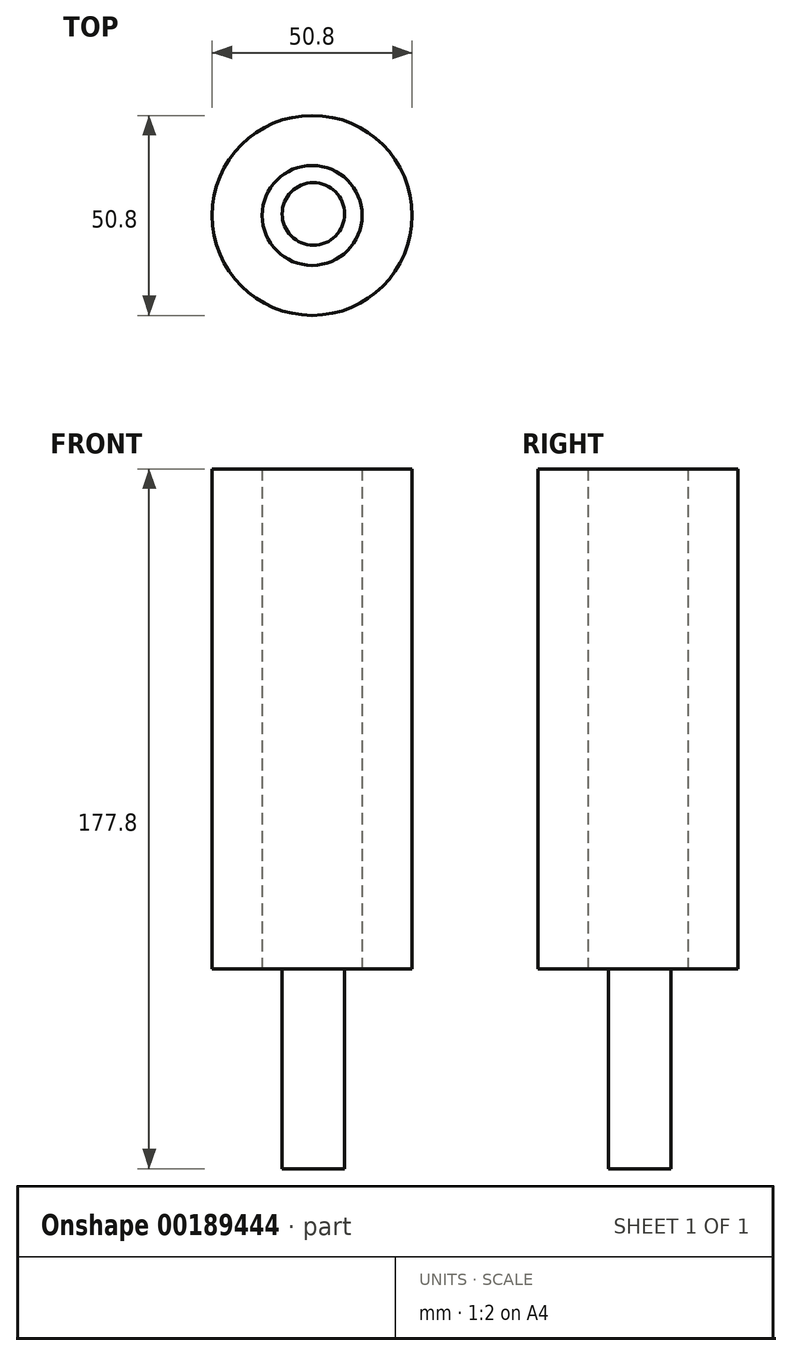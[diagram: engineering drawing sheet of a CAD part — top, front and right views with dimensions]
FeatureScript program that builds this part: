
annotation { "Feature Type Name" : "Feature", "Feature Type Description" : "" }
export const myFeature = defineFeature(function(context is Context, id is Id, definition is map)
    precondition{}
    {
        {
            var Q0;
            Q0=qCreatedBy(makeId("Top.planeOp"),FACE);
            var sketch = newSketch(context, id + "F0", { "sketchPlane" : qUnion([Q0])});
            skCircle(sketch, "E0", {"center": v(-29.64, 14.83) * mm, "radius": 25.4 * mm});
            skSolve(sketch);
        }
        {
            var Q0;
            Q0 = qSketchRegion(id + "F0", true);
            extrude(context, id + "F1", {"entities" : qUnion([Q0]), "depth" : 127 * mm});
        }
        {
            var Q0;
            Q0=sQuery(id+"F0.wireOp",VERTEX,"E0.center");
            var Q1;
            Q1=makeQuery(id+"F1.opExtrude","SWEPT_BODY",BODY,{"disambiguationData":[OSD([sQuery(id+"F0.wireOp",EDGE,"E0")])]});
            hole(context, id + "F2", {"style" : HoleStyle.SIMPLE, "endStyle" : HoleEndStyle.BLIND, "oppositeDirection" : true, "holeDiameter" : 25.4 * mm, "holeDepth" : 76.2 * mm, "locations" : qUnion([Q0]), "scope" : qUnion([Q1])});
        }
        {
            var Q0;
            Q0=makeQuery(id+"F1.opExtrude","CAP_FACE",FACE,{"disambiguationData":[OSD([sQuery(id+"F0.wireOp",EDGE,"E0")])],"isStart":false});
            var sketch = newSketch(context, id + "F3", { "sketchPlane" : qUnion([Q0])});
            skSolve(sketch);
        }
        {
            var Q0;
            Q0=makeQuery(id+"F0.imprint","IMPRINT",FACE,{"disambiguationData":[TD([[makeQuery(id+"F0.imprint","IMPRINT",EDGE,{"derivedFrom":sQuery(id+"F0.wireOp",EDGE,"E0")}),1.0]])]});
            var sketch = newSketch(context, id + "F4", { "sketchPlane" : qUnion([Q0])});
            skCircle(sketch, "E1", {"center": v(-29.32, 15.2) * mm, "radius": 7.94 * mm});
            skSolve(sketch);
        }
        {
            var Q0;
            Q0 = qSketchRegion(id + "F4", true);
            extrude(context, id + "F5", {"entities" : qUnion([Q0]), "operationType" : NewBodyOperationType.ADD, "oppositeDirection" : true, "depth" : 50.8 * mm});
        }
        {
            var Q0;
            Q0=makeQuery(id+"F3.imprint","IMPRINT",FACE,{"disambiguationData":[TD([[makeQuery(id+"F3.imprint","IMPRINT",EDGE,{"derivedFrom":makeQuery(id+"F1.opExtrude","CAP_EDGE",EDGE,{"disambiguationData":[OSD([sQuery(id+"F0.wireOp",EDGE,"E0")])],"isStart":false})}),1.0]])]});
            var sketch = newSketch(context, id + "F6", { "sketchPlane" : qUnion([Q0])});
            skPoint(sketch, "E2", {"position": v(-29.64, 14.83) * mm});
            skSolve(sketch);
        }
        {
            var Q0;
            Q0=sQuery(id+"F0.wireOp",VERTEX,"E0.center");
            var Q1;
            Q1=sQuery(id+"F6.wireOp",VERTEX,"E2");
            var Q2;
            Q2=makeQuery(id+"F1.opExtrude","SWEPT_BODY",BODY,{"disambiguationData":[OSD([sQuery(id+"F0.wireOp",EDGE,"E0")])]});
            hole(context, id + "F7", {"style" : HoleStyle.SIMPLE, "endStyle" : HoleEndStyle.BLIND, "holeDiameter" : 25.4 * mm, "holeDepth" : 76.2 * mm, "locations" : qUnion([Q0, Q1]), "scope" : qUnion([Q2])});
        }
    });
